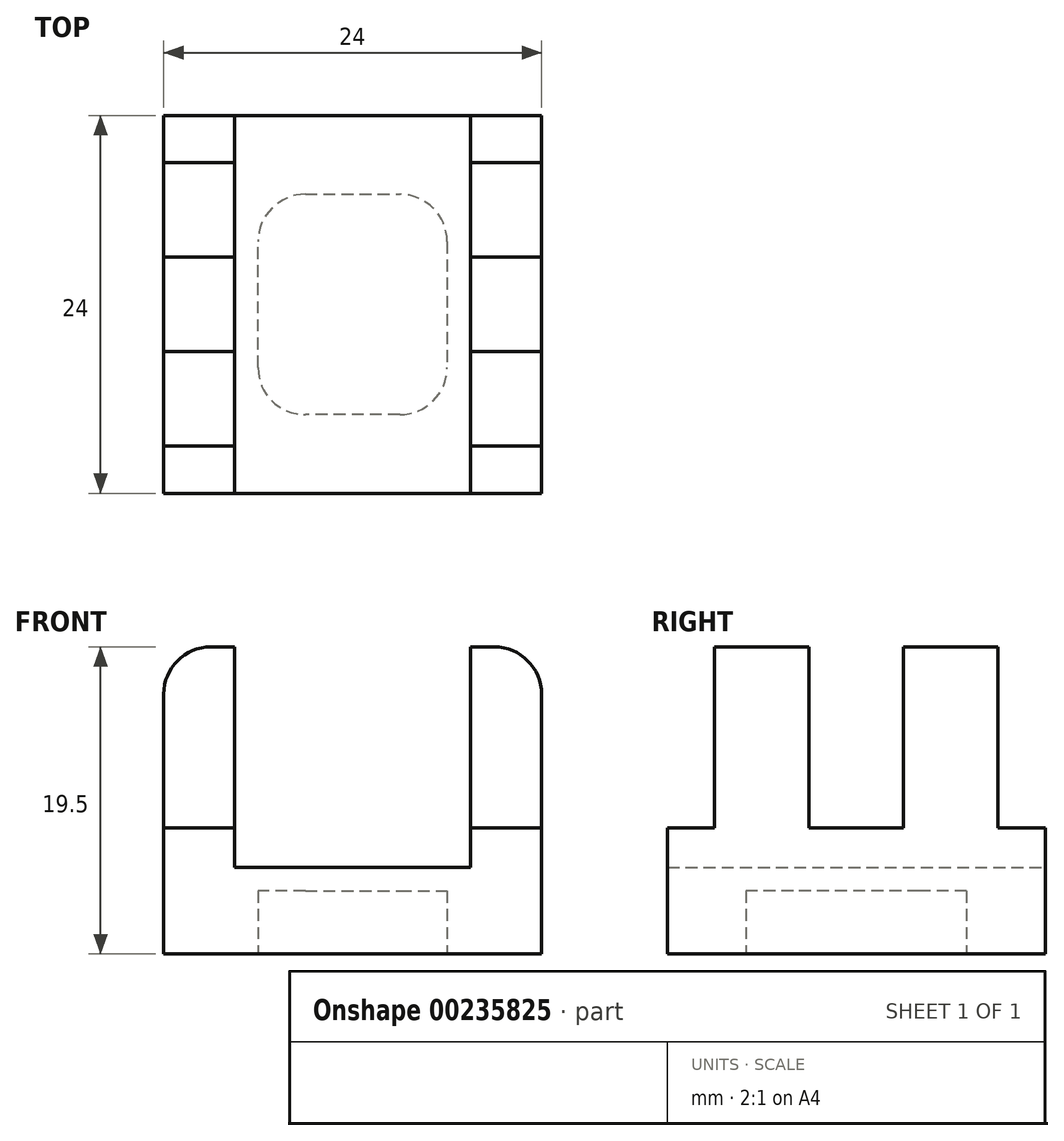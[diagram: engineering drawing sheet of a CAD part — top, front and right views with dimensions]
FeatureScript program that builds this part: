
annotation { "Feature Type Name" : "Feature", "Feature Type Description" : "" }
export const myFeature = defineFeature(function(context is Context, id is Id, definition is map)
    precondition{}
    {
        {
            var Q0;
            Q0=qCreatedBy(makeId("Top.planeOp"),FACE);
            var sketch = newSketch(context, id + "F0", { "sketchPlane" : qUnion([Q0])});
            skLineSegment(sketch, "E0", {"start": v(12, 0) * mm, "end": v(12, 12) * mm});
            skLineSegment(sketch, "E1", {"start": v(12, 12) * mm, "end": v(-12, 12) * mm});
            skLineSegment(sketch, "E2", {"start": v(-12, 12) * mm, "end": v(-12, -12) * mm});
            skLineSegment(sketch, "E3", {"start": v(-12, -12) * mm, "end": v(12, -12) * mm});
            skLineSegment(sketch, "E4", {"start": v(12, -12) * mm, "end": v(12, 0) * mm});
            skSolve(sketch);
        }
        {
            var Q0;
            Q0=makeQuery(id+"F0.imprint","IMPRINT",FACE,{"disambiguationData":[TD([[makeQuery(id+"F0.imprint","IMPRINT",EDGE,{"derivedFrom":sQuery(id+"F0.wireOp",EDGE,"E0")}),1.0]])]});
            extrude(context, id + "F1", {"entities" : qUnion([Q0]), "depth" : 5.5 * mm});
        }
        {
            var Q0;
            Q0=makeQuery(id+"F1.opExtrude","CAP_FACE",FACE,{"disambiguationData":[OSD([sQuery(id+"F0.wireOp",EDGE,"E0"),sQuery(id+"F0.wireOp",EDGE,"E1"),sQuery(id+"F0.wireOp",EDGE,"E2"),sQuery(id+"F0.wireOp",EDGE,"E3"),sQuery(id+"F0.wireOp",EDGE,"E4")])],"isStart":false});
            var sketch = newSketch(context, id + "F2", { "sketchPlane" : qUnion([Q0])});
            skLineSegment(sketch, "E5", {"start": v(-12, -12) * mm, "end": v(-7.5, -12) * mm});
            skLineSegment(sketch, "E6", {"start": v(-7.5, -12) * mm, "end": v(-7.5, 12) * mm});
            skLineSegment(sketch, "E7", {"start": v(-7.5, 12) * mm, "end": v(-12, 12) * mm});
            skLineSegment(sketch, "E8", {"start": v(-12, 12) * mm, "end": v(-12, -12) * mm});
            skLineSegment(sketch, "E9.MirrorCS", {"start": v(7.5, -12) * mm, "end": v(7.5, 12) * mm});
            skLineSegment(sketch, "E10.MirrorCS", {"start": v(7.5, 12) * mm, "end": v(12, 12) * mm});
            skLineSegment(sketch, "E11.MirrorCS", {"start": v(12, 12) * mm, "end": v(12, -12) * mm});
            skLineSegment(sketch, "E12.MirrorCS", {"start": v(12, -12) * mm, "end": v(7.5, -12) * mm});
            skSolve(sketch);
        }
        {
            var Q0;
            Q0=makeQuery(id+"F2.imprint","IMPRINT",FACE,{"disambiguationData":[TD([[makeQuery(id+"F2.imprint","IMPRINT",EDGE,{"derivedFrom":sQuery(id+"F2.wireOp",EDGE,"E5")}),1.0]])]});
            var Q1;
            Q1=makeQuery(id+"F2.imprint","IMPRINT",FACE,{"disambiguationData":[TD([[makeQuery(id+"F2.imprint","IMPRINT",EDGE,{"derivedFrom":sQuery(id+"F2.wireOp",EDGE,"E9.MirrorCS")}),-1.0]])]});
            extrude(context, id + "F3", {"entities" : qUnion([Q0, Q1]), "operationType" : NewBodyOperationType.ADD, "depth" : 2.5 * mm});
        }
        {
            var Q0;
            Q0=makeQuery(id+"F3.opExtrude","CAP_FACE",FACE,{"disambiguationData":[OSD([sQuery(id+"F2.wireOp",EDGE,"E5"),sQuery(id+"F2.wireOp",EDGE,"E6"),sQuery(id+"F2.wireOp",EDGE,"E7"),sQuery(id+"F2.wireOp",EDGE,"E8")])],"isStart":false});
            var sketch = newSketch(context, id + "F4", { "sketchPlane" : qUnion([Q0])});
            skLineSegment(sketch, "E13", {"start": v(0, 0) * mm, "end": v(-12, 0) * mm});
            skLineSegment(sketch, "E14", {"start": v(-12, 0) * mm, "end": v(-12, 3) * mm});
            skLineSegment(sketch, "E15", {"start": v(-12, 3) * mm, "end": v(-7.5, 3) * mm});
            skLineSegment(sketch, "E16", {"start": v(-7.5, 3) * mm, "end": v(-7.5, 9) * mm});
            skLineSegment(sketch, "E17", {"start": v(-7.5, 9) * mm, "end": v(-12, 9) * mm});
            skLineSegment(sketch, "E18", {"start": v(-12, 9) * mm, "end": v(-12, 3) * mm});
            skLineSegment(sketch, "E19.MirrorCS", {"start": v(-12, -3) * mm, "end": v(-7.5, -3) * mm});
            skLineSegment(sketch, "E20.MirrorCS", {"start": v(-7.5, -9) * mm, "end": v(-12, -9) * mm});
            skLineSegment(sketch, "E21.MirrorCS", {"start": v(-7.5, -3) * mm, "end": v(-7.5, -9) * mm});
            skLineSegment(sketch, "E22.MirrorCS", {"start": v(-12, -9) * mm, "end": v(-12, -3) * mm});
            skLineSegment(sketch, "E23.MirrorCS", {"start": v(12, 3) * mm, "end": v(7.5, 3) * mm});
            skLineSegment(sketch, "E24.MirrorCS", {"start": v(7.5, 9) * mm, "end": v(12, 9) * mm});
            skLineSegment(sketch, "E25.MirrorCS", {"start": v(12, 9) * mm, "end": v(12, 3) * mm});
            skLineSegment(sketch, "E26.MirrorCS", {"start": v(7.5, 3) * mm, "end": v(7.5, 9) * mm});
            skLineSegment(sketch, "E27.MirrorCS", {"start": v(12, -3) * mm, "end": v(7.5, -3) * mm});
            skLineSegment(sketch, "E28.MirrorCS", {"start": v(12, -9) * mm, "end": v(12, -3) * mm});
            skLineSegment(sketch, "E29.MirrorCS", {"start": v(7.5, -9) * mm, "end": v(12, -9) * mm});
            skLineSegment(sketch, "E30.MirrorCS", {"start": v(7.5, -3) * mm, "end": v(7.5, -9) * mm});
            skSolve(sketch);
        }
        {
            var Q0;
            Q0=makeQuery(id+"F4.imprint","IMPRINT",FACE,{"disambiguationData":[TD([[makeQuery(id+"F4.imprint","IMPRINT",EDGE,{"derivedFrom":sQuery(id+"F4.wireOp",EDGE,"E15")}),1.0]])]});
            var Q1;
            Q1=makeQuery(id+"F4.imprint","IMPRINT",FACE,{"disambiguationData":[TD([[makeQuery(id+"F4.imprint","IMPRINT",EDGE,{"derivedFrom":sQuery(id+"F4.wireOp",EDGE,"E19.MirrorCS")}),-1.0]])]});
            var Q2;
            Q2=makeQuery(id+"F4.imprint","IMPRINT",FACE,{"disambiguationData":[TD([[makeQuery(id+"F4.imprint","IMPRINT",EDGE,{"derivedFrom":sQuery(id+"F4.wireOp",EDGE,"E23.MirrorCS")}),-1.0]])]});
            var Q3;
            Q3=makeQuery(id+"F4.imprint","IMPRINT",FACE,{"disambiguationData":[TD([[makeQuery(id+"F4.imprint","IMPRINT",EDGE,{"derivedFrom":sQuery(id+"F4.wireOp",EDGE,"E27.MirrorCS")}),1.0]])]});
            extrude(context, id + "F5", {"entities" : qUnion([Q0, Q1, Q2, Q3]), "operationType" : NewBodyOperationType.ADD, "depth" : 11.5 * mm});
        }
        {
            var Q0;
            Q0=makeQuery(id+"F5.opExtrude","CAP_EDGE",EDGE,{"disambiguationData":[OSD([sQuery(id+"F4.wireOp",EDGE,"E28.MirrorCS")])],"isStart":false});
            var Q1;
            Q1=makeQuery(id+"F5.opExtrude","CAP_EDGE",EDGE,{"disambiguationData":[OSD([sQuery(id+"F4.wireOp",EDGE,"E25.MirrorCS")])],"isStart":false});
            var Q2;
            Q2=makeQuery(id+"F5.opExtrude","CAP_EDGE",EDGE,{"disambiguationData":[OSD([sQuery(id+"F4.wireOp",EDGE,"E18")])],"isStart":false});
            var Q3;
            Q3=makeQuery(id+"F5.opExtrude","CAP_EDGE",EDGE,{"disambiguationData":[OSD([sQuery(id+"F4.wireOp",EDGE,"E22.MirrorCS")])],"isStart":false});
            fillet(context, id + "F6", {"entities" : qUnion([Q0, Q1, Q2, Q3]), "radius" : 3 * mm, "tangentPropagation" : true, "allowEdgeOverflow" : false});
        }
        {
            var Q0;
            Q0=makeQuery(id+"F1.opExtrude","CAP_FACE",FACE,{"disambiguationData":[OSD([sQuery(id+"F0.wireOp",EDGE,"E0"),sQuery(id+"F0.wireOp",EDGE,"E1"),sQuery(id+"F0.wireOp",EDGE,"E2"),sQuery(id+"F0.wireOp",EDGE,"E3"),sQuery(id+"F0.wireOp",EDGE,"E4")])],"isStart":true});
            var sketch = newSketch(context, id + "F7", { "sketchPlane" : qUnion([Q0])});
            skLineSegment(sketch, "E31", {"start": v(0, -7) * mm, "end": v(3, -7) * mm});
            skLineSegment(sketch, "E32", {"start": v(6, -4) * mm, "end": v(6, 4) * mm});
            skLineSegment(sketch, "E33", {"start": v(3, 7) * mm, "end": v(-3, 7) * mm});
            skLineSegment(sketch, "E34", {"start": v(-6, 4) * mm, "end": v(-6, -4) * mm});
            skLineSegment(sketch, "E35", {"start": v(-3, -7) * mm, "end": v(0, -7) * mm});
            skPoint(sketch, "E36.visualSharp", {"position": v(6, 7) * mm});
            skArc(sketch, "E36.filletArc", {"start": v(6, 4) * mm, "mid": v(5.12, 6.12) * mm, "end": v(3, 7) * mm});
            skPoint(sketch, "E37.visualSharp", {"position": v(6, -7) * mm});
            skArc(sketch, "E37.filletArc", {"start": v(3, -7) * mm, "mid": v(5.12, -6.12) * mm, "end": v(6, -4) * mm});
            skPoint(sketch, "E38.visualSharp", {"position": v(-6, -7) * mm});
            skArc(sketch, "E38.filletArc", {"start": v(-6, -4) * mm, "mid": v(-5.12, -6.12) * mm, "end": v(-3, -7) * mm});
            skPoint(sketch, "E39.visualSharp", {"position": v(-6, 7) * mm});
            skArc(sketch, "E39.filletArc", {"start": v(-3, 7) * mm, "mid": v(-5.12, 6.12) * mm, "end": v(-6, 4) * mm});
            skSolve(sketch);
        }
        {
            var Q0;
            Q0=makeQuery(id+"F7.imprint","IMPRINT",FACE,{"disambiguationData":[TD([[makeQuery(id+"F7.imprint","IMPRINT",EDGE,{"derivedFrom":sQuery(id+"F7.wireOp",EDGE,"E31")}),1.0]])]});
            extrude(context, id + "F8", {"entities" : qUnion([Q0]), "operationType" : NewBodyOperationType.REMOVE, "oppositeDirection" : true, "depth" : 4 * mm});
        }
    });
